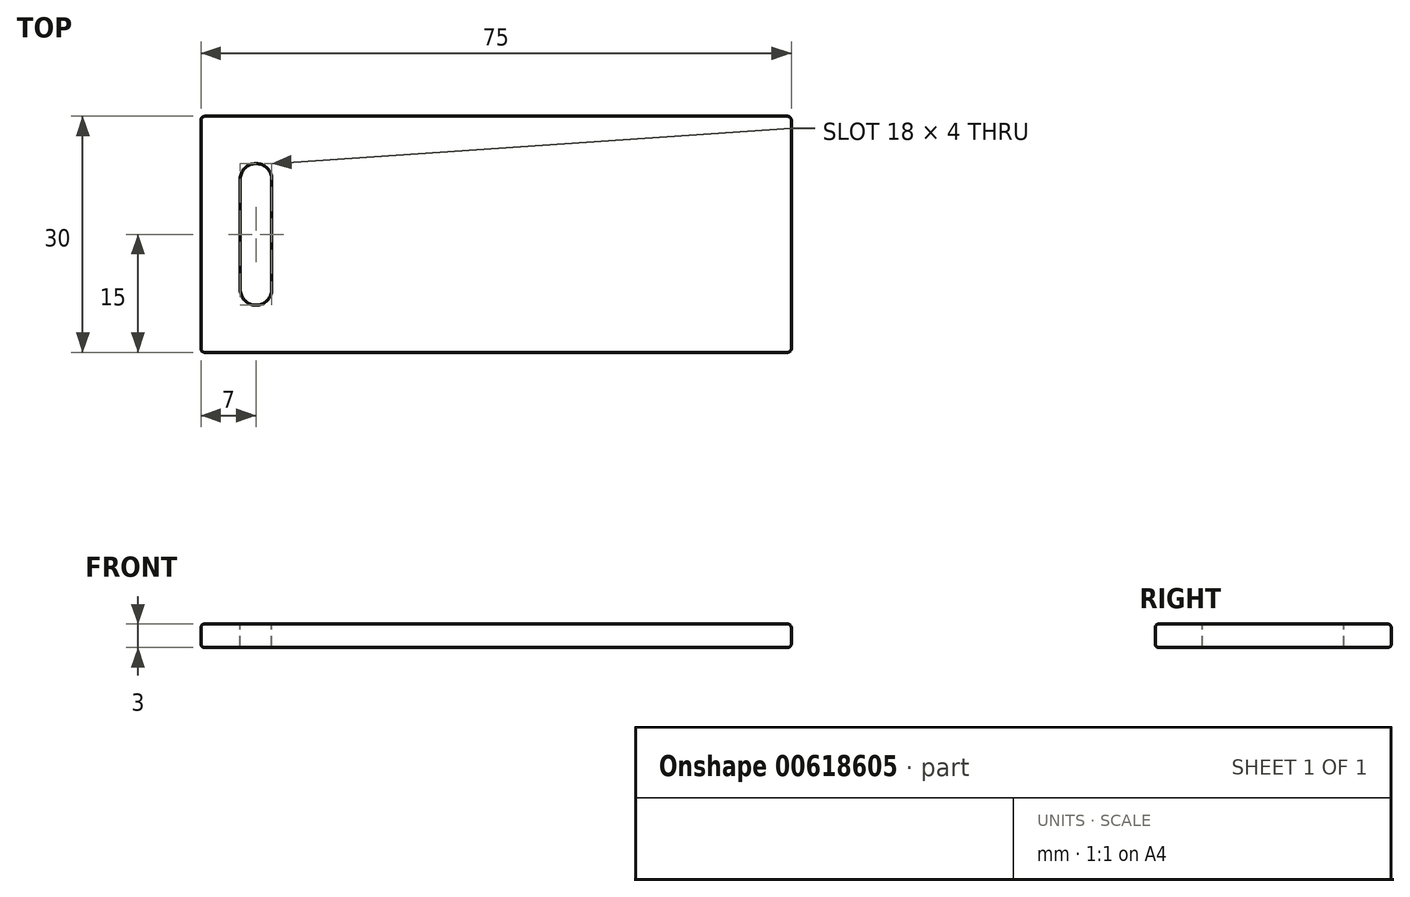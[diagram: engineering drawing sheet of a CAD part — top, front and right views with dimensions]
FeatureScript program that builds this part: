
annotation { "Feature Type Name" : "Feature", "Feature Type Description" : "" }
export const myFeature = defineFeature(function(context is Context, id is Id, definition is map)
    precondition{}
    {
        {
            var Q0;
            Q0=qCreatedBy(makeId("Top.planeOp"),FACE);
            var sketch = newSketch(context, id + "F0", { "sketchPlane" : qUnion([Q0])});
            skLineSegment(sketch, "E0.bottom", {"start": v(0, 0) * mm, "end": v(75, 0) * mm});
            skLineSegment(sketch, "E0.top", {"start": v(0, 30) * mm, "end": v(75, 30) * mm});
            skLineSegment(sketch, "E0.left", {"start": v(0, 0) * mm, "end": v(0, 30) * mm});
            skLineSegment(sketch, "E0.right", {"start": v(75, 0) * mm, "end": v(75, 30) * mm});
            skLineSegment(sketch, "E1", {"start": v(37.5, 30) * mm, "end": v(37.5, 0) * mm, "construction": true});
            skLineSegment(sketch, "E2", {"start": v(0, 15) * mm, "end": v(75, 15) * mm, "construction": true});
            skSolve(sketch);
        }
        {
            var Q0;
            Q0=makeQuery(id+"F0.imprint","IMPRINT",FACE,{"disambiguationData":[TD([[makeQuery(id+"F0.imprint","IMPRINT",EDGE,{"derivedFrom":sQuery(id+"F0.wireOp",EDGE,"E0.bottom")}),1.0]])]});
            extrude(context, id + "F1", {"entities" : qUnion([Q0]), "depth" : 3 * mm, "offsetDistance" : 25 * mm});
        }
        {
            var Q0;
            Q0=makeQuery(id+"F1.opExtrude","CAP_FACE",FACE,{"disambiguationData":[OSD([sQuery(id+"F0.wireOp",EDGE,"E0.bottom"),sQuery(id+"F0.wireOp",EDGE,"E0.top"),sQuery(id+"F0.wireOp",EDGE,"E0.left"),sQuery(id+"F0.wireOp",EDGE,"E0.right")])],"isStart":false});
            var sketch = newSketch(context, id + "F2", { "sketchPlane" : qUnion([Q0])});
            skLineSegment(sketch, "E3.bottom", {"start": v(5, 15) * mm, "end": v(9, 15) * mm});
            skLineSegment(sketch, "E3.top", {"start": v(5, 8) * mm, "end": v(9, 8) * mm});
            skLineSegment(sketch, "E3.left", {"start": v(5, 15) * mm, "end": v(5, 8) * mm});
            skLineSegment(sketch, "E3.right", {"start": v(9, 15) * mm, "end": v(9, 8) * mm});
            skArc(sketch, "E4", {"start": v(5, 8) * mm, "mid": v(7, 6) * mm, "end": v(9, 8) * mm});
            skLineSegment(sketch, "E5.MirrorCS", {"start": v(5, 15) * mm, "end": v(5, 22) * mm});
            skLineSegment(sketch, "E6.MirrorCS", {"start": v(9, 15) * mm, "end": v(9, 22) * mm});
            skArc(sketch, "E7.MirrorCS", {"start": v(5, 22) * mm, "mid": v(7, 24) * mm, "end": v(9, 22) * mm});
            skSolve(sketch);
        }
        {
            var Q0;
            Q0 = qSketchRegion(id + "F2", true);
            extrude(context, id + "F3", {"entities" : qUnion([Q0]), "operationType" : NewBodyOperationType.REMOVE, "oppositeDirection" : true, "depth" : 25 * mm, "offsetDistance" : 25 * mm});
        }
        {
            var Q0;
            Q0=makeQuery(id+"F1.opExtrude","CAP_EDGE",EDGE,{"disambiguationData":[OSD([sQuery(id+"F0.wireOp",EDGE,"E0.top")])],"isStart":false});
            var Q1;
            Q1=makeQuery(id+"F1.opExtrude","CAP_EDGE",EDGE,{"disambiguationData":[OSD([sQuery(id+"F0.wireOp",EDGE,"E0.left")])],"isStart":false});
            var Q2;
            Q2=makeQuery(id+"F1.opExtrude","CAP_EDGE",EDGE,{"disambiguationData":[OSD([sQuery(id+"F0.wireOp",EDGE,"E0.bottom")])],"isStart":false});
            var Q3;
            Q3=makeQuery(id+"F1.opExtrude","CAP_EDGE",EDGE,{"disambiguationData":[OSD([sQuery(id+"F0.wireOp",EDGE,"E0.right")])],"isStart":false});
            var Q4;
            Q4=makeQuery(id+"F1.opExtrude","CAP_EDGE",EDGE,{"disambiguationData":[OSD([sQuery(id+"F0.wireOp",EDGE,"E0.right")])],"isStart":true});
            var Q5;
            Q5=makeQuery(id+"F1.opExtrude","CAP_EDGE",EDGE,{"disambiguationData":[OSD([sQuery(id+"F0.wireOp",EDGE,"E0.bottom")])],"isStart":true});
            var Q6;
            Q6=makeQuery(id+"F1.opExtrude","CAP_EDGE",EDGE,{"disambiguationData":[OSD([sQuery(id+"F0.wireOp",EDGE,"E0.top")])],"isStart":true});
            var Q7;
            Q7=makeQuery(id+"F1.opExtrude","CAP_EDGE",EDGE,{"disambiguationData":[OSD([sQuery(id+"F0.wireOp",EDGE,"E0.left")])],"isStart":true});
            var Q8;
            Q8=makeQuery(id+"F1.opExtrude","SWEPT_EDGE",EDGE,{"disambiguationData":[OSD([sQuery(id+"F0.wireOp",EDGE,"E0.bottom"),sQuery(id+"F0.wireOp",EDGE,"E0.right")])]});
            var Q9;
            Q9=makeQuery(id+"F1.opExtrude","SWEPT_EDGE",EDGE,{"disambiguationData":[OSD([sQuery(id+"F0.wireOp",EDGE,"E0.top"),sQuery(id+"F0.wireOp",EDGE,"E0.right")])]});
            var Q10;
            Q10=makeQuery(id+"F1.opExtrude","SWEPT_EDGE",EDGE,{"disambiguationData":[OSD([sQuery(id+"F0.wireOp",EDGE,"E0.top"),sQuery(id+"F0.wireOp",EDGE,"E0.left")])]});
            var Q11;
            Q11=makeQuery(id+"F1.opExtrude","SWEPT_EDGE",EDGE,{"disambiguationData":[OSD([sQuery(id+"F0.wireOp",EDGE,"E0.bottom"),sQuery(id+"F0.wireOp",EDGE,"E0.left")])]});
            fillet(context, id + "F4", {"entities" : qUnion([Q0, Q1, Q2, Q3, Q4, Q5, Q6, Q7, Q8, Q9, Q10, Q11]), "radius" : .5 * mm, "tangentPropagation" : true, "allowEdgeOverflow" : false});
        }
    });
